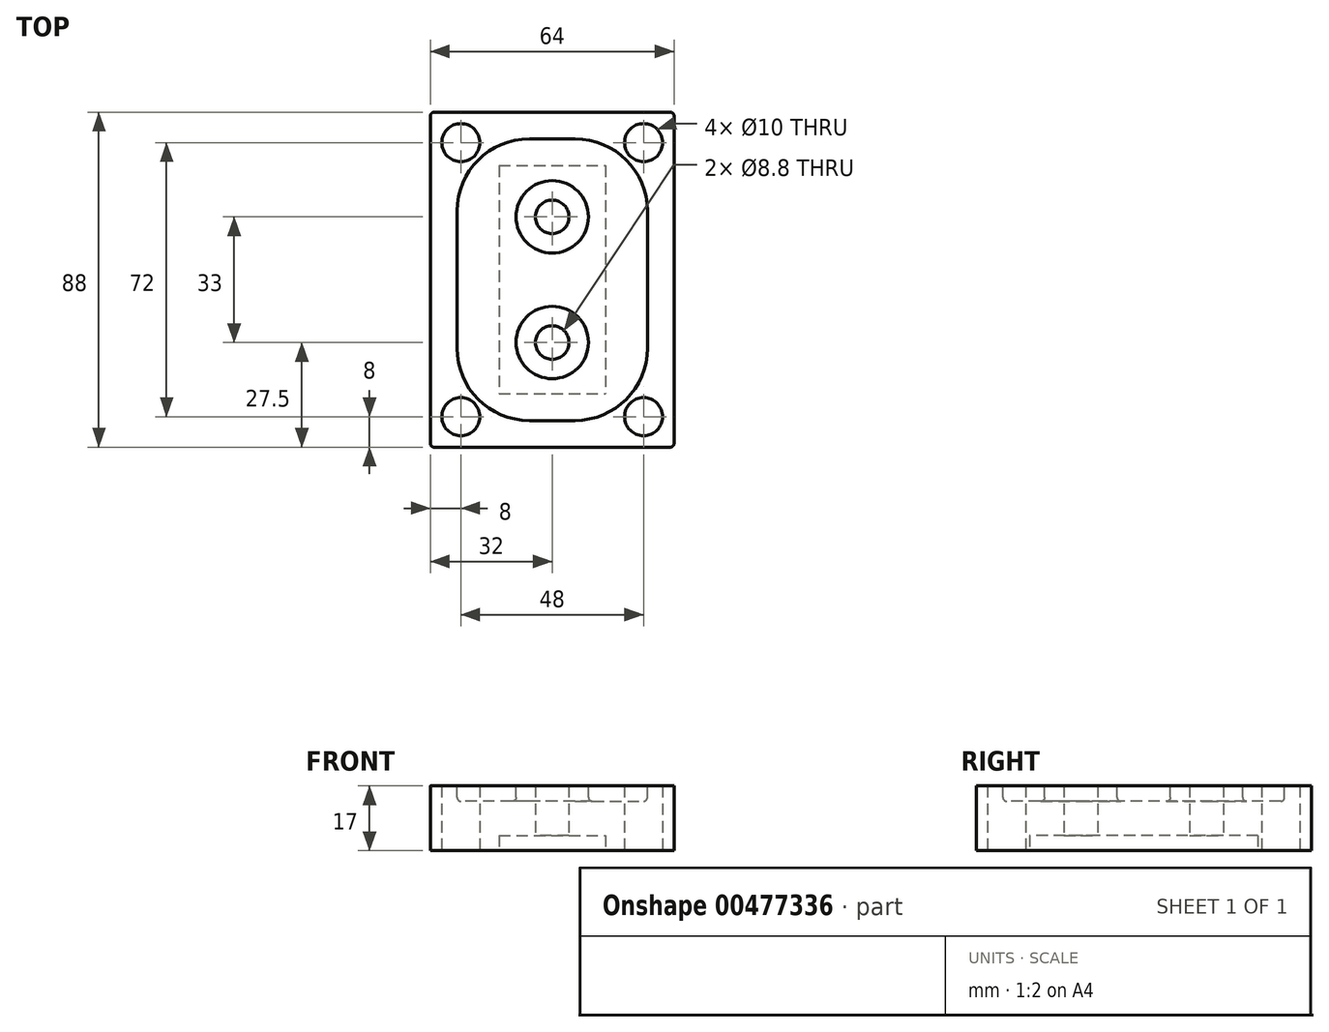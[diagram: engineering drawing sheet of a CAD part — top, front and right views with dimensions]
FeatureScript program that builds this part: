
annotation { "Feature Type Name" : "Feature", "Feature Type Description" : "" }
export const myFeature = defineFeature(function(context is Context, id is Id, definition is map)
    precondition{}
    {
        {
            var Q0;
            Q0=qCreatedBy(makeId("Top.planeOp"),FACE);
            var sketch = newSketch(context, id + "F0", { "sketchPlane" : qUnion([Q0])});
            skLineSegment(sketch, "E0.bottom", {"start": v(-32, 44) * mm, "end": v(32, 44) * mm});
            skLineSegment(sketch, "E0.top", {"start": v(-32, -44) * mm, "end": v(32, -44) * mm});
            skLineSegment(sketch, "E0.left", {"start": v(-32, 44) * mm, "end": v(-32, -44) * mm});
            skLineSegment(sketch, "E0.right", {"start": v(32, 44) * mm, "end": v(32, -44) * mm});
            skSolve(sketch);
        }
        {
            var Q0;
            Q0=makeQuery(id+"F0.imprint","IMPRINT",FACE,{"disambiguationData":[TD([[makeQuery(id+"F0.imprint","IMPRINT",EDGE,{"derivedFrom":sQuery(id+"F0.wireOp",EDGE,"E0.bottom")}),-1.0]])]});
            extrude(context, id + "F1", {"entities" : qUnion([Q0]), "depth" : 17 * mm});
        }
        {
            var Q0;
            Q0=qCreatedBy(makeId("Top.planeOp"),FACE);
            var sketch = newSketch(context, id + "F2", { "sketchPlane" : qUnion([Q0])});
            skPoint(sketch, "E1", {"position": v(-24, 36) * mm});
            skPoint(sketch, "E2.MirrorP", {"position": v(24, 36) * mm});
            skPoint(sketch, "E3.MirrorP", {"position": v(-24, -36) * mm});
            skPoint(sketch, "E4.MirrorP", {"position": v(24, -36) * mm});
            skSolve(sketch);
        }
        {
            var Q0;
            Q0=sQuery(id+"F2.wireOp",VERTEX,"E1");
            var Q1;
            Q1=sQuery(id+"F2.wireOp",VERTEX,"E2.MirrorP");
            var Q2;
            Q2=sQuery(id+"F2.wireOp",VERTEX,"E4.MirrorP");
            var Q3;
            Q3=sQuery(id+"F2.wireOp",VERTEX,"E3.MirrorP");
            var Q4;
            Q4=makeQuery(id+"F1.opExtrude","SWEPT_BODY",BODY,{"disambiguationData":[OSD([sQuery(id+"F0.wireOp",EDGE,"E0.bottom"),sQuery(id+"F0.wireOp",EDGE,"E0.top"),sQuery(id+"F0.wireOp",EDGE,"E0.left"),sQuery(id+"F0.wireOp",EDGE,"E0.right")])]});
            hole(context, id + "F3", {"style" : HoleStyle.SIMPLE, "endStyle" : HoleEndStyle.THROUGH, "oppositeDirection" : true, "holeDiameter" : 10 * mm, "isTappedThrough" : true, "tappedDepth" : 12 * mm, "tapClearance" : 3, "locations" : qUnion([Q0, Q1, Q2, Q3]), "scope" : qUnion([Q4])});
        }
        {
            var Q0;
            Q0=qCreatedBy(makeId("Top.planeOp"),FACE);
            var sketch = newSketch(context, id + "F4", { "sketchPlane" : qUnion([Q0])});
            skLineSegment(sketch, "E5.bottom", {"start": v(-14, 30) * mm, "end": v(14, 30) * mm});
            skLineSegment(sketch, "E5.top", {"start": v(-14, -30) * mm, "end": v(14, -30) * mm});
            skLineSegment(sketch, "E5.left", {"start": v(-14, 30) * mm, "end": v(-14, -30) * mm});
            skLineSegment(sketch, "E5.right", {"start": v(14, 30) * mm, "end": v(14, -30) * mm});
            skSolve(sketch);
        }
        {
            var Q0;
            Q0 = qSketchRegion(id + "F4", true);
            extrude(context, id + "F5", {"entities" : qUnion([Q0]), "operationType" : NewBodyOperationType.REMOVE, "depth" : 4 * mm});
        }
        {
            var Q0;
            Q0=qCreatedBy(makeId("Top.planeOp"),FACE);
            var sketch = newSketch(context, id + "F6", { "sketchPlane" : qUnion([Q0])});
            skPoint(sketch, "E6", {"position": v(0, -16.5) * mm});
            skPoint(sketch, "E7.MirrorP", {"position": v(0, 16.5) * mm});
            skSolve(sketch);
        }
        {
            var Q0;
            Q0=sQuery(id+"F6.wireOp",VERTEX,"E6");
            var Q1;
            Q1=sQuery(id+"F6.wireOp",VERTEX,"E7.MirrorP");
            var Q2;
            Q2=makeQuery(id+"F1.opExtrude","SWEPT_BODY",BODY,{"disambiguationData":[OSD([sQuery(id+"F0.wireOp",EDGE,"E0.bottom"),sQuery(id+"F0.wireOp",EDGE,"E0.top"),sQuery(id+"F0.wireOp",EDGE,"E0.left"),sQuery(id+"F0.wireOp",EDGE,"E0.right")])]});
            hole(context, id + "F7", {"style" : HoleStyle.SIMPLE, "endStyle" : HoleEndStyle.THROUGH, "oppositeDirection" : true, "standardTappedOrClearance" : lookupTablePath({ "standard" : "ISO", "fit" : "Normal", "size" : "M8", "type" : "Clearance" }), "standardBlindInLast" : lookupTablePath({ "fit" : "Standard", "standard" : "ISO", "size" : "M8", "type" : "Clearance" }), "holeDiameter" : 8.8 * mm, "isTappedThrough" : true, "tappedDepth" : 12 * mm, "tapClearance" : 3, "locations" : qUnion([Q0, Q1]), "scope" : qUnion([Q2])});
        }
        {
            var Q0;
            Q0=makeQuery(id+"F1.opExtrude","CAP_FACE",FACE,{"disambiguationData":[OSD([sQuery(id+"F0.wireOp",EDGE,"E0.bottom"),sQuery(id+"F0.wireOp",EDGE,"E0.top"),sQuery(id+"F0.wireOp",EDGE,"E0.left"),sQuery(id+"F0.wireOp",EDGE,"E0.right")])],"isStart":false});
            var sketch = newSketch(context, id + "F8", { "sketchPlane" : qUnion([Q0])});
            skLineSegment(sketch, "E8", {"start": v(-25, 18) * mm, "end": v(-25, 0) * mm});
            skArc(sketch, "E9", {"start": v(-6, 37) * mm, "mid": v(-19.44, 31.44) * mm, "end": v(-25, 18) * mm});
            skLineSegment(sketch, "E10", {"start": v(-6, 37) * mm, "end": v(0, 37) * mm});
            skLineSegment(sketch, "E11.MirrorCS", {"start": v(6, 37) * mm, "end": v(0, 37) * mm});
            skArc(sketch, "E12.MirrorCS", {"start": v(6, 37) * mm, "mid": v(19.44, 31.44) * mm, "end": v(25, 18) * mm});
            skLineSegment(sketch, "E13.MirrorCS", {"start": v(25, 18) * mm, "end": v(25, 0) * mm});
            skLineSegment(sketch, "E14.MirrorCS", {"start": v(-25, -18) * mm, "end": v(-25, 0) * mm});
            skArc(sketch, "E15.MirrorCS", {"start": v(-6, -37) * mm, "mid": v(-19.44, -31.44) * mm, "end": v(-25, -18) * mm});
            skLineSegment(sketch, "E16.MirrorCS", {"start": v(-6, -37) * mm, "end": v(0, -37) * mm});
            skLineSegment(sketch, "E17.MirrorCS", {"start": v(6, -37) * mm, "end": v(0, -37) * mm});
            skArc(sketch, "E18.MirrorCS", {"start": v(6, -37) * mm, "mid": v(19.44, -31.44) * mm, "end": v(25, -18) * mm});
            skLineSegment(sketch, "E19.MirrorCS", {"start": v(25, -18) * mm, "end": v(25, 0) * mm});
            skCircle(sketch, "E20", {"center": v(0, 16.5) * mm, "radius": 9.5 * mm});
            skCircle(sketch, "E21.MirrorC", {"center": v(0, -16.5) * mm, "radius": 9.5 * mm});
            skSolve(sketch);
        }
        {
            var Q0;
            Q0 = qSketchRegion(id + "F8", true);
            extrude(context, id + "F9", {"entities" : qUnion([Q0]), "operationType" : NewBodyOperationType.REMOVE, "oppositeDirection" : true, "depth" : 4 * mm});
        }
        {
            var Q0;
            Q0=makeQuery(id+"F9.boolean.opBoolean","COPY",FACE,{"derivedFrom":makeQuery(id+"F9.opExtrude","CAP_FACE",FACE,{"disambiguationData":[OSD([sQuery(id+"F8.wireOp",EDGE,"E8"),sQuery(id+"F8.wireOp",EDGE,"E9"),sQuery(id+"F8.wireOp",EDGE,"E10"),sQuery(id+"F8.wireOp",EDGE,"E11.MirrorCS"),sQuery(id+"F8.wireOp",EDGE,"E12.MirrorCS"),sQuery(id+"F8.wireOp",EDGE,"E13.MirrorCS"),sQuery(id+"F8.wireOp",EDGE,"E14.MirrorCS"),sQuery(id+"F8.wireOp",EDGE,"E15.MirrorCS"),sQuery(id+"F8.wireOp",EDGE,"E16.MirrorCS"),sQuery(id+"F8.wireOp",EDGE,"E17.MirrorCS"),sQuery(id+"F8.wireOp",EDGE,"E18.MirrorCS"),sQuery(id+"F8.wireOp",EDGE,"E19.MirrorCS"),sQuery(id+"F8.wireOp",EDGE,"E20"),sQuery(id+"F8.wireOp",EDGE,"E21.MirrorC")])],"isStart":false})});
            var Q1;
            Q1=makeQuery(id+"F9.boolean.opBoolean","SPLIT",FACE,{"disambiguationData":[TD([makeQuery(id+"F7.hole-1.boolean.opBoolean","COPY",FACE,{"derivedFrom":makeQuery(id+"F7.hole-1.opRevolve","SWEPT_FACE",FACE,{"disambiguationData":[OSD([sQuery(id+"F7.hole-1.sketch.wireOp",EDGE,"core_line_2")])]})})])],"derivedFrom":makeQuery(id+"F1.opExtrude","CAP_FACE",FACE,{"disambiguationData":[OSD([sQuery(id+"F0.wireOp",EDGE,"E0.bottom"),sQuery(id+"F0.wireOp",EDGE,"E0.top"),sQuery(id+"F0.wireOp",EDGE,"E0.left"),sQuery(id+"F0.wireOp",EDGE,"E0.right")])],"isStart":false})});
            var Q2;
            Q2=makeQuery(id+"F9.boolean.opBoolean","SPLIT",FACE,{"disambiguationData":[TD([makeQuery(id+"F7.hole-0.boolean.opBoolean","COPY",FACE,{"derivedFrom":makeQuery(id+"F7.hole-0.opRevolve","SWEPT_FACE",FACE,{"disambiguationData":[OSD([sQuery(id+"F7.hole-0.sketch.wireOp",EDGE,"core_line_2")])]})})])],"derivedFrom":makeQuery(id+"F1.opExtrude","CAP_FACE",FACE,{"disambiguationData":[OSD([sQuery(id+"F0.wireOp",EDGE,"E0.bottom"),sQuery(id+"F0.wireOp",EDGE,"E0.top"),sQuery(id+"F0.wireOp",EDGE,"E0.left"),sQuery(id+"F0.wireOp",EDGE,"E0.right")])],"isStart":false})});
            fillet(context, id + "F10", {"entities" : qUnion([Q0, Q1, Q2]), "radius" : 1 * mm, "tangentPropagation" : true, "allowEdgeOverflow" : false});
        }
        {
            var Q0;
            Q0=makeQuery(id+"F1.opExtrude","SWEPT_EDGE",EDGE,{"disambiguationData":[OSD([sQuery(id+"F0.wireOp",EDGE,"E0.bottom"),sQuery(id+"F0.wireOp",EDGE,"E0.left")])]});
            var Q1;
            Q1=makeQuery(id+"F1.opExtrude","SWEPT_EDGE",EDGE,{"disambiguationData":[OSD([sQuery(id+"F0.wireOp",EDGE,"E0.top"),sQuery(id+"F0.wireOp",EDGE,"E0.left")])]});
            var Q2;
            Q2=makeQuery(id+"F1.opExtrude","SWEPT_EDGE",EDGE,{"disambiguationData":[OSD([sQuery(id+"F0.wireOp",EDGE,"E0.bottom"),sQuery(id+"F0.wireOp",EDGE,"E0.right")])]});
            var Q3;
            Q3=makeQuery(id+"F1.opExtrude","SWEPT_EDGE",EDGE,{"disambiguationData":[OSD([sQuery(id+"F0.wireOp",EDGE,"E0.top"),sQuery(id+"F0.wireOp",EDGE,"E0.right")])]});
            fillet(context, id + "F11", {"entities" : qUnion([Q0, Q1, Q2, Q3]), "radius" : 1 * mm, "tangentPropagation" : true, "allowEdgeOverflow" : false});
        }
    });
